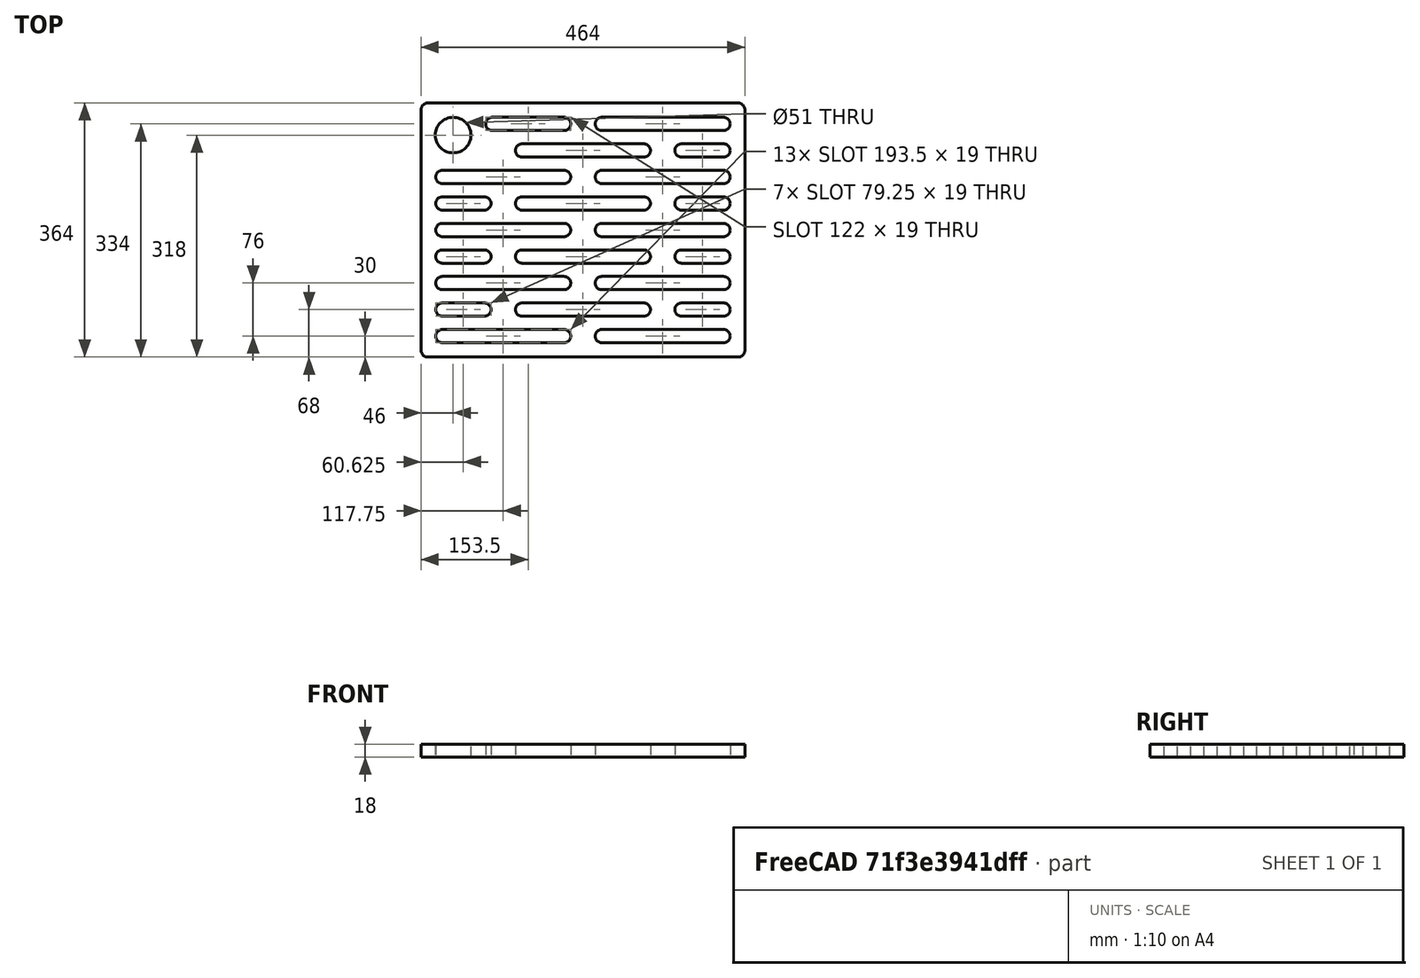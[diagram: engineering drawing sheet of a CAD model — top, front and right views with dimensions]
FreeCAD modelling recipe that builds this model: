
FCSTD DOCUMENT  (FreeCAD 0.18R4 (GitTag))
Label: shelf
License: All rights reserved
LicenseURL: http://en.wikipedia.org/wiki/All_rights_reserved
objects: Sketcher::SketchObject×1, PartDesign::Pad×1, PartDesign::Body×1
note: 4 computed .brp shape members not serialized (recipe doc carries the construction recipe); baked Part::Feature solids carry a one-line shape summary decoded from their .brp

FEATURE [Sketcher::SketchObject] Sketch
  MapMode = 5
  Support = -> [XY_Plane]
  sketch-geometry (93):
    g0: ArcOfCircle CenterX=-9.5 CenterY=9.5 CenterZ=0 NormalX=0 NormalY=0 NormalZ=1 AngleXU=0 Radius=9.5 StartAngle=4.71239 EndAngle=6.28319
    g1: ArcOfCircle CenterX=-9.5 CenterY=354.5 CenterZ=0 NormalX=0 NormalY=0 NormalZ=1 AngleXU=0 Radius=9.5 StartAngle=2.54933e-09 EndAngle=1.5708
    g2: ArcOfCircle CenterX=-454.5 CenterY=354.5 CenterZ=0 NormalX=0 NormalY=0 NormalZ=1 AngleXU=0 Radius=9.5 StartAngle=1.5708 EndAngle=3.14159
    g3: ArcOfCircle CenterX=-454.5 CenterY=9.5 CenterZ=0 NormalX=0 NormalY=0 NormalZ=1 AngleXU=0 Radius=9.5 StartAngle=3.14159 EndAngle=4.71239
    g4: LineSegment StartX=-454.5 StartY=0 StartZ=0 EndX=-9.5 EndY=0 EndZ=0
    g5: LineSegment StartX=0 StartY=9.5 StartZ=0 EndX=0 EndY=354.5 EndZ=0
    g6: LineSegment StartX=-9.5 StartY=364 StartZ=0 EndX=-454.5 EndY=364 EndZ=0
    g7: LineSegment StartX=-464 StartY=354.5 StartZ=0 EndX=-464 EndY=9.5 EndZ=0
    g8: Circle CenterX=-418 CenterY=318 CenterZ=0 NormalX=0 NormalY=0 NormalZ=1 AngleXU=0 Radius=25.5
    g9: ArcOfCircle CenterX=-205 CenterY=30 CenterZ=0 NormalX=0 NormalY=0 NormalZ=1 AngleXU=0 Radius=9.5 StartAngle=1.5708 EndAngle=4.71239
    g10: ArcOfCircle CenterX=-30.5 CenterY=30 CenterZ=0 NormalX=0 NormalY=0 NormalZ=1 AngleXU=0 Radius=9.5 StartAngle=4.71239 EndAngle=7.85398
    g11: LineSegment StartX=-205 StartY=20.5 StartZ=0 EndX=-30.5 EndY=20.5 EndZ=0
    g12: LineSegment StartX=-205 StartY=39.5 StartZ=0 EndX=-30.5 EndY=39.5 EndZ=0
    g13: ArcOfCircle CenterX=-90.75 CenterY=68 CenterZ=0 NormalX=0 NormalY=0 NormalZ=1 AngleXU=0 Radius=9.5 StartAngle=1.5708 EndAngle=4.71239
    g14: ArcOfCircle CenterX=-30.5 CenterY=68 CenterZ=0 NormalX=0 NormalY=0 NormalZ=1 AngleXU=0 Radius=9.5 StartAngle=4.71239 EndAngle=7.85398
    g15: LineSegment StartX=-90.75 StartY=58.5 StartZ=0 EndX=-30.5 EndY=58.5 EndZ=0
    g16: LineSegment StartX=-90.75 StartY=77.5 StartZ=0 EndX=-30.5 EndY=77.5 EndZ=0
    g17: ArcOfCircle CenterX=-205 CenterY=106 CenterZ=0 NormalX=0 NormalY=0 NormalZ=1 AngleXU=0 Radius=9.5 StartAngle=1.5708 EndAngle=4.71239
    g18: ArcOfCircle CenterX=-30.5 CenterY=106 CenterZ=0 NormalX=0 NormalY=0 NormalZ=1 AngleXU=0 Radius=9.5 StartAngle=4.71239 EndAngle=7.85398
    g19: LineSegment StartX=-205 StartY=96.5 StartZ=0 EndX=-30.5 EndY=96.5 EndZ=0
    g20: LineSegment StartX=-205 StartY=115.5 StartZ=0 EndX=-30.5 EndY=115.5 EndZ=0
    g21: ArcOfCircle CenterX=-90.75 CenterY=144 CenterZ=0 NormalX=0 NormalY=0 NormalZ=1 AngleXU=0 Radius=9.5 StartAngle=1.5708 EndAngle=4.71239
    g22: ArcOfCircle CenterX=-30.5 CenterY=144 CenterZ=0 NormalX=0 NormalY=0 NormalZ=1 AngleXU=0 Radius=9.5 StartAngle=4.71239 EndAngle=7.85398
    g23: LineSegment StartX=-90.75 StartY=134.5 StartZ=0 EndX=-30.5 EndY=134.5 EndZ=0
    g24: LineSegment StartX=-90.75 StartY=153.5 StartZ=0 EndX=-30.5 EndY=153.5 EndZ=0
    g25: ArcOfCircle CenterX=-205 CenterY=182 CenterZ=0 NormalX=0 NormalY=0 NormalZ=1 AngleXU=0 Radius=9.5 StartAngle=1.5708 EndAngle=4.71239
    g26: ArcOfCircle CenterX=-30.5 CenterY=182 CenterZ=0 NormalX=0 NormalY=0 NormalZ=1 AngleXU=0 Radius=9.5 StartAngle=4.71239 EndAngle=7.85398
    g27: LineSegment StartX=-205 StartY=172.5 StartZ=0 EndX=-30.5 EndY=172.5 EndZ=0
    g28: LineSegment StartX=-205 StartY=191.5 StartZ=0 EndX=-30.5 EndY=191.5 EndZ=0
    g29: ArcOfCircle CenterX=-90.75 CenterY=220 CenterZ=0 NormalX=0 NormalY=0 NormalZ=1 AngleXU=0 Radius=9.5 StartAngle=1.5708 EndAngle=4.71239
    g30: ArcOfCircle CenterX=-30.5 CenterY=220 CenterZ=0 NormalX=0 NormalY=0 NormalZ=1 AngleXU=0 Radius=9.5 StartAngle=4.71239 EndAngle=7.85398
    g31: LineSegment StartX=-90.75 StartY=210.5 StartZ=0 EndX=-30.5 EndY=210.5 EndZ=0
    g32: LineSegment StartX=-90.75 StartY=229.5 StartZ=0 EndX=-30.5 EndY=229.5 EndZ=0
    g33: ArcOfCircle CenterX=-205 CenterY=258 CenterZ=0 NormalX=0 NormalY=0 NormalZ=1 AngleXU=0 Radius=9.5 StartAngle=1.5708 EndAngle=4.71239
    g34: ArcOfCircle CenterX=-30.5 CenterY=258 CenterZ=0 NormalX=0 NormalY=0 NormalZ=1 AngleXU=0 Radius=9.5 StartAngle=4.71239 EndAngle=7.85398
    g35: LineSegment StartX=-205 StartY=248.5 StartZ=0 EndX=-30.5 EndY=248.5 EndZ=0
    g36: LineSegment StartX=-205 StartY=267.5 StartZ=0 EndX=-30.5 EndY=267.5 EndZ=0
    g37: ArcOfCircle CenterX=-90.75 CenterY=296 CenterZ=0 NormalX=0 NormalY=0 NormalZ=1 AngleXU=0 Radius=9.5 StartAngle=1.5708 EndAngle=4.71239
    g38: ArcOfCircle CenterX=-30.5 CenterY=296 CenterZ=0 NormalX=0 NormalY=0 NormalZ=1 AngleXU=0 Radius=9.5 StartAngle=4.71239 EndAngle=7.85398
    g39: LineSegment StartX=-90.75 StartY=286.5 StartZ=0 EndX=-30.5 EndY=286.5 EndZ=0
    g40: LineSegment StartX=-90.75 StartY=305.5 StartZ=0 EndX=-30.5 EndY=305.5 EndZ=0
    g41: ArcOfCircle CenterX=-259 CenterY=30 CenterZ=0 NormalX=0 NormalY=0 NormalZ=1 AngleXU=0 Radius=9.5 StartAngle=4.71239 EndAngle=7.85398
    g42: ArcOfCircle CenterX=-433.5 CenterY=30 CenterZ=0 NormalX=0 NormalY=0 NormalZ=1 AngleXU=0 Radius=9.5 StartAngle=1.5708 EndAngle=4.71239
    g43: LineSegment StartX=-259 StartY=39.5 StartZ=0 EndX=-433.5 EndY=39.5 EndZ=0
    g44: LineSegment StartX=-259 StartY=20.5 StartZ=0 EndX=-433.5 EndY=20.5 EndZ=0
    g45: ArcOfCircle CenterX=-433.5 CenterY=68 CenterZ=0 NormalX=0 NormalY=0 NormalZ=1 AngleXU=0 Radius=9.5 StartAngle=1.5708 EndAngle=4.71239
    g46: ArcOfCircle CenterX=-373.25 CenterY=68 CenterZ=0 NormalX=0 NormalY=0 NormalZ=1 AngleXU=0 Radius=9.5 StartAngle=4.71239 EndAngle=7.85398
    g47: LineSegment StartX=-433.5 StartY=58.5 StartZ=0 EndX=-373.25 EndY=58.5 EndZ=0
    g48: LineSegment StartX=-433.5 StartY=77.5 StartZ=0 EndX=-373.25 EndY=77.5 EndZ=0
    g49: ArcOfCircle CenterX=-319.25 CenterY=68 CenterZ=0 NormalX=0 NormalY=0 NormalZ=1 AngleXU=0 Radius=9.5 StartAngle=1.5708 EndAngle=4.71239
    g50: ArcOfCircle CenterX=-144.75 CenterY=68 CenterZ=0 NormalX=0 NormalY=0 NormalZ=1 AngleXU=0 Radius=9.5 StartAngle=4.71239 EndAngle=7.85398
    g51: LineSegment StartX=-319.25 StartY=58.5 StartZ=0 EndX=-144.75 EndY=58.5 EndZ=0
    g52: LineSegment StartX=-319.25 StartY=77.5 StartZ=0 EndX=-144.75 EndY=77.5 EndZ=0
    g53: ArcOfCircle CenterX=-433.5 CenterY=106 CenterZ=0 NormalX=0 NormalY=0 NormalZ=1 AngleXU=0 Radius=9.5 StartAngle=1.5708 EndAngle=4.71239
    g54: ArcOfCircle CenterX=-259 CenterY=106 CenterZ=0 NormalX=0 NormalY=0 NormalZ=1 AngleXU=0 Radius=9.5 StartAngle=4.71239 EndAngle=7.85398
    g55: LineSegment StartX=-433.5 StartY=96.5 StartZ=0 EndX=-259 EndY=96.5 EndZ=0
    g56: LineSegment StartX=-433.5 StartY=115.5 StartZ=0 EndX=-259 EndY=115.5 EndZ=0
    g57: ArcOfCircle CenterX=-319.25 CenterY=144 CenterZ=0 NormalX=0 NormalY=0 NormalZ=1 AngleXU=0 Radius=9.5 StartAngle=1.5708 EndAngle=4.71239
    g58: ArcOfCircle CenterX=-144.75 CenterY=144 CenterZ=0 NormalX=0 NormalY=0 NormalZ=1 AngleXU=0 Radius=9.5 StartAngle=4.71239 EndAngle=7.85398
    g59: LineSegment StartX=-319.25 StartY=134.5 StartZ=0 EndX=-144.75 EndY=134.5 EndZ=0
    g60: LineSegment StartX=-319.25 StartY=153.5 StartZ=0 EndX=-144.75 EndY=153.5 EndZ=0
    g61: ArcOfCircle CenterX=-373.25 CenterY=144 CenterZ=0 NormalX=0 NormalY=0 NormalZ=1 AngleXU=0 Radius=9.5 StartAngle=4.71239 EndAngle=7.85398
    g62: ArcOfCircle CenterX=-433.5 CenterY=144 CenterZ=0 NormalX=0 NormalY=0 NormalZ=1 AngleXU=0 Radius=9.5 StartAngle=1.5708 EndAngle=4.71239
    g63: LineSegment StartX=-373.25 StartY=153.5 StartZ=0 EndX=-433.5 EndY=153.5 EndZ=0
    g64: LineSegment StartX=-373.25 StartY=134.5 StartZ=0 EndX=-433.5 EndY=134.5 EndZ=0
    g65: ArcOfCircle CenterX=-259 CenterY=182 CenterZ=0 NormalX=0 NormalY=0 NormalZ=1 AngleXU=0 Radius=9.5 StartAngle=4.71239 EndAngle=7.85398
    g66: ArcOfCircle CenterX=-433.5 CenterY=182 CenterZ=0 NormalX=0 NormalY=0 NormalZ=1 AngleXU=0 Radius=9.5 StartAngle=1.5708 EndAngle=4.71239
    g67: LineSegment StartX=-259 StartY=191.5 StartZ=0 EndX=-433.5 EndY=191.5 EndZ=0
    g68: LineSegment StartX=-259 StartY=172.5 StartZ=0 EndX=-433.5 EndY=172.5 EndZ=0
    g69: ArcOfCircle CenterX=-144.75 CenterY=220 CenterZ=0 NormalX=0 NormalY=0 NormalZ=1 AngleXU=0 Radius=9.5 StartAngle=4.71239 EndAngle=7.85398
    g70: ArcOfCircle CenterX=-319.25 CenterY=220 CenterZ=0 NormalX=0 NormalY=0 NormalZ=1 AngleXU=0 Radius=9.5 StartAngle=1.5708 EndAngle=4.71239
    g71: LineSegment StartX=-144.75 StartY=229.5 StartZ=0 EndX=-319.25 EndY=229.5 EndZ=0
    g72: LineSegment StartX=-144.75 StartY=210.5 StartZ=0 EndX=-319.25 EndY=210.5 EndZ=0
    g73: ArcOfCircle CenterX=-373.25 CenterY=220 CenterZ=0 NormalX=0 NormalY=0 NormalZ=1 AngleXU=0 Radius=9.5 StartAngle=4.71239 EndAngle=7.85398
    g74: ArcOfCircle CenterX=-433.5 CenterY=220 CenterZ=0 NormalX=0 NormalY=0 NormalZ=1 AngleXU=0 Radius=9.5 StartAngle=1.5708 EndAngle=4.71239
    g75: LineSegment StartX=-373.25 StartY=229.5 StartZ=0 EndX=-433.5 EndY=229.5 EndZ=0
    g76: LineSegment StartX=-373.25 StartY=210.5 StartZ=0 EndX=-433.5 EndY=210.5 EndZ=0
    g77: ArcOfCircle CenterX=-259 CenterY=258 CenterZ=0 NormalX=0 NormalY=0 NormalZ=1 AngleXU=0 Radius=9.5 StartAngle=4.71239 EndAngle=7.85398
    g78: ArcOfCircle CenterX=-433.5 CenterY=258 CenterZ=0 NormalX=0 NormalY=0 NormalZ=1 AngleXU=0 Radius=9.5 StartAngle=1.5708 EndAngle=4.71239
    g79: LineSegment StartX=-259 StartY=267.5 StartZ=0 EndX=-433.5 EndY=267.5 EndZ=0
    g80: LineSegment StartX=-259 StartY=248.5 StartZ=0 EndX=-433.5 EndY=248.5 EndZ=0
    g81: ArcOfCircle CenterX=-319.25 CenterY=296 CenterZ=0 NormalX=0 NormalY=0 NormalZ=1 AngleXU=0 Radius=9.5 StartAngle=1.5708 EndAngle=4.71239
    g82: ArcOfCircle CenterX=-144.75 CenterY=296 CenterZ=0 NormalX=0 NormalY=0 NormalZ=1 AngleXU=0 Radius=9.5 StartAngle=4.71239 EndAngle=7.85398
    g83: LineSegment StartX=-319.25 StartY=286.5 StartZ=0 EndX=-144.75 EndY=286.5 EndZ=0
    g84: LineSegment StartX=-319.25 StartY=305.5 StartZ=0 EndX=-144.75 EndY=305.5 EndZ=0
    g85: ArcOfCircle CenterX=-30.5 CenterY=334 CenterZ=0 NormalX=0 NormalY=0 NormalZ=1 AngleXU=0 Radius=9.5 StartAngle=4.71239 EndAngle=7.85398
    g86: ArcOfCircle CenterX=-205 CenterY=334 CenterZ=0 NormalX=0 NormalY=0 NormalZ=1 AngleXU=0 Radius=9.5 StartAngle=1.5708 EndAngle=4.71239
    g87: LineSegment StartX=-30.5 StartY=343.5 StartZ=0 EndX=-205 EndY=343.5 EndZ=0
    g88: LineSegment StartX=-30.5 StartY=324.5 StartZ=0 EndX=-205 EndY=324.5 EndZ=0
    g89: ArcOfCircle CenterX=-259 CenterY=334 CenterZ=0 NormalX=0 NormalY=0 NormalZ=1 AngleXU=0 Radius=9.5 StartAngle=4.71239 EndAngle=7.85398
    g90: ArcOfCircle CenterX=-362 CenterY=334 CenterZ=0 NormalX=0 NormalY=0 NormalZ=1 AngleXU=0 Radius=9.5 StartAngle=1.5708 EndAngle=4.71239
    g91: LineSegment StartX=-259 StartY=343.5 StartZ=0 EndX=-362 EndY=343.5 EndZ=0
    g92: LineSegment StartX=-259 StartY=324.5 StartZ=0 EndX=-362 EndY=324.5 EndZ=0
  constraints (241):
    c: Horizontal(g6)
    c: Horizontal(g4)
    c: Vertical(g5)
    c: Vertical(g7)
    c: Coincident(g6,g1)
    c: Coincident(g1,g5)
    c: Coincident(g0,g5)
    c: Coincident(g0,g4)
    c: Coincident(g4,g3)
    c: Coincident(g3,g7)
    c: Coincident(g2,g6)
    c: Coincident(g2,g7)
    c: DistanceX(g0,g0) = 9.5
    c: DistanceY(g0,g0) = 9.5
    c: Radius(g0) = 9.5
    c: DistanceX(g1,g1) = 9.5
    c: DistanceY(g1,g1) = 9.5
    c: Radius(g1) = 9.5
    c: DistanceX(g2,g2) = 9.5
    c: DistanceY(g2,g2) = 9.5
    c: Radius(g2) = 9.5
    c: DistanceX(g3,g3) = 9.5
    c: DistanceY(g3,g3) = 9.5
    c: Radius(g3) = 9.5
    c: DistanceX(g0,g-1) = 0
    c: DistanceY(g-1,g0) = 0
    c: Diameter(g8) = 51
    c: DistanceX(g3,g0) = 464
    c: DistanceY(g0,g1) = 364
    c: DistanceX(g2,g8) = 46
    c: Tangent(g9,g12) = 1.5708
    c: Tangent(g9,g11) = -1.5708
    c: Tangent(g11,g10) = -1.5708
    c: Tangent(g12,g10) = 1.5708
    c: Horizontal(g11)
    c: Equal(g9,g10)
    c: Tangent(g13,g16) = 1.5708
    c: Tangent(g13,g15) = -1.5708
    c: Tangent(g15,g14) = -1.5708
    c: Tangent(g16,g14) = 1.5708
    c: Horizontal(g15)
    c: Equal(g13,g14)
    c: Tangent(g17,g20) = 1.5708
    c: Tangent(g17,g19) = -1.5708
    c: Tangent(g19,g18) = -1.5708
    c: Tangent(g20,g18) = 1.5708
    c: Horizontal(g19)
    c: Equal(g17,g18)
    c: Tangent(g21,g24) = 1.5708
    c: Tangent(g21,g23) = -1.5708
    c: Tangent(g23,g22) = -1.5708
    c: Tangent(g24,g22) = 1.5708
    c: Horizontal(g23)
    c: Equal(g21,g22)
    c: Tangent(g25,g28) = 1.5708
    c: Tangent(g25,g27) = -1.5708
    c: Tangent(g27,g26) = -1.5708
    c: Tangent(g28,g26) = 1.5708
    c: Horizontal(g27)
    c: Equal(g25,g26)
    c: Tangent(g29,g32) = 1.5708
    c: Tangent(g29,g31) = -1.5708
    c: Tangent(g31,g30) = -1.5708
    c: Tangent(g32,g30) = 1.5708
    c: Horizontal(g31)
    c: Equal(g29,g30)
    c: Tangent(g33,g36) = 1.5708
    c: Tangent(g33,g35) = -1.5708
    c: Tangent(g35,g34) = -1.5708
    c: Tangent(g36,g34) = 1.5708
    c: Horizontal(g35)
    c: Equal(g33,g34)
    c: DistanceY(g10,g10) = 19
    c: DistanceY(g14,g14) = 19
    c: DistanceY(g18,g18) = 19
    c: DistanceY(g22,g22) = 19
    c: DistanceY(g26,g26) = 19
    c: DistanceY(g30,g30) = 19
    c: DistanceY(g34,g34) = 19
    c: DistanceY(g10,g14) = 19
    c: DistanceY(g14,g18) = 19
    c: DistanceY(g18,g22) = 19
    c: DistanceY(g22,g26) = 19
    c: DistanceY(g26,g30) = 19
    c: DistanceY(g30,g34) = 19
    c: Tangent(g37,g40) = 1.5708
    c: Tangent(g37,g39) = -1.5708
    c: Tangent(g39,g38) = -1.5708
    c: Tangent(g40,g38) = 1.5708
    c: Horizontal(g39)
    c: Equal(g37,g38)
    c: DistanceY(g34,g38) = 19
    c: DistanceY(g38,g38) = 19
    c: DistanceY(g0,g10) = 20.5
    c: DistanceX(g10,g0) = 30.5
    c: DistanceX(g14,g10) = 0
    c: DistanceX(g18,g14) = 0
    c: DistanceX(g22,g18) = 0
    c: DistanceX(g26,g22) = 0
    c: DistanceX(g26,g30) = 0
    c: DistanceX(g34,g30) = 0
    c: DistanceX(g38,g34) = 0
    c: Tangent(g41,g44) = 1.5708
    c: Tangent(g41,g43) = -1.5708
    c: Tangent(g43,g42) = -1.5708
    c: Tangent(g44,g42) = 1.5708
    c: Horizontal(g43)
    c: Equal(g41,g42)
    c: DistanceY(g42,g42) = 19
    c: DistanceY(g3,g42) = 20.5
    c: DistanceX(g3,g42) = 30.5
    c: DistanceX(g9,g10) = 174.5
    c: DistanceX(g44,g44) = 174.5
    c: Tangent(g45,g48) = 1.5708
    c: Tangent(g45,g47) = -1.5708
    c: Tangent(g47,g46) = -1.5708
    c: Tangent(g48,g46) = 1.5708
    c: Horizontal(g47)
    c: Equal(g45,g46)
    c: Tangent(g49,g52) = 1.5708
    c: Tangent(g49,g51) = -1.5708
    c: Tangent(g51,g50) = -1.5708
    c: Tangent(g52,g50) = 1.5708
    c: Horizontal(g51)
    c: Equal(g49,g50)
    c: DistanceY(g9,g50) = 19
    c: DistanceY(g50,g50) = 19
    c: DistanceY(g42,g45) = 19
    c: DistanceY(g45,g45) = 19
    c: DistanceX(g45,g42) = 0
    c: DistanceX(g50,g13) = 54
    c: DistanceX(g46,g49) = 54
    c: DistanceX(g45,g46) = 60.25
    c: DistanceX(g52,g52) = 174.5
    c: Tangent(g53,g56) = 1.5708
    c: Tangent(g53,g55) = -1.5708
    c: Tangent(g55,g54) = -1.5708
    c: Tangent(g56,g54) = 1.5708
    c: Horizontal(g55)
    c: Equal(g53,g54)
    c: DistanceY(g45,g53) = 19
    c: DistanceY(g53,g53) = 19
    c: DistanceX(g53,g45) = 0
    c: DistanceX(g54,g41) = 0
    c: DistanceX(g9,g17) = 0
    c: Tangent(g57,g60) = 1.5708
    c: Tangent(g57,g59) = -1.5708
    c: Tangent(g59,g58) = -1.5708
    c: Tangent(g60,g58) = 1.5708
    c: Horizontal(g59)
    c: Equal(g57,g58)
    c: Tangent(g61,g64) = 1.5708
    c: Tangent(g61,g63) = -1.5708
    c: Tangent(g63,g62) = -1.5708
    c: Tangent(g64,g62) = 1.5708
    c: Horizontal(g63)
    c: Equal(g61,g62)
    c: Tangent(g65,g68) = 1.5708
    c: Tangent(g65,g67) = -1.5708
    c: Tangent(g67,g66) = -1.5708
    c: Tangent(g68,g66) = 1.5708
    c: Horizontal(g67)
    c: Equal(g65,g66)
    c: Tangent(g69,g72) = 1.5708
    c: Tangent(g69,g71) = -1.5708
    c: Tangent(g71,g70) = -1.5708
    c: Tangent(g72,g70) = 1.5708
    c: Horizontal(g71)
    c: Equal(g69,g70)
    c: Tangent(g73,g76) = 1.5708
    c: Tangent(g73,g75) = -1.5708
    c: Tangent(g75,g74) = -1.5708
    c: Tangent(g76,g74) = 1.5708
    c: Horizontal(g75)
    c: Equal(g73,g74)
    c: Tangent(g77,g80) = 1.5708
    c: Tangent(g77,g79) = -1.5708
    c: Tangent(g79,g78) = -1.5708
    c: Tangent(g80,g78) = 1.5708
    c: Horizontal(g79)
    c: Equal(g77,g78)
    c: DistanceY(g58,g58) = 19
    c: DistanceY(g58,g21) = 0
    c: DistanceY(g57,g61) = 0
    c: DistanceY(g61,g61) = 19
    c: DistanceX(g62,g53) = 0
    c: DistanceX(g46,g61) = 0
    c: DistanceX(g49,g57) = 0
    c: DistanceX(g50,g58) = 0
    c: DistanceX(g21,g13) = 0
    c: DistanceY(g62,g66) = 19
    c: DistanceY(g66,g66) = 19
    c: DistanceX(g17,g25) = 0
    c: DistanceX(g65,g54) = 0
    c: DistanceY(g66,g74) = 19
    c: DistanceY(g74,g74) = 19
    c: DistanceY(g70,g70) = 19
    c: DistanceY(g70,g73) = 0
    c: DistanceX(g61,g73) = 0
    c: DistanceX(g57,g70) = 0
    c: DistanceX(g69,g58) = 0
    c: DistanceX(g29,g21) = 0
    c: DistanceY(g78,g78) = 19
    c: DistanceY(g33,g77) = 0
    c: DistanceX(g33,g25) = 0
    c: DistanceX(g65,g77) = 0
    c: Tangent(g81,g84) = 1.5708
    c: Tangent(g81,g83) = -1.5708
    c: Tangent(g83,g82) = -1.5708
    c: Tangent(g84,g82) = 1.5708
    c: Horizontal(g83)
    c: Equal(g81,g82)
    c: DistanceY(g82,g82) = 19
    c: DistanceY(g37,g82) = 0
    c: DistanceX(g29,g37) = 0
    c: DistanceX(g69,g82) = 0
    c: Tangent(g85,g88) = 1.5708
    c: Tangent(g85,g87) = -1.5708
    c: Tangent(g87,g86) = -1.5708
    c: Tangent(g88,g86) = 1.5708
    c: Horizontal(g87)
    c: Equal(g85,g86)
    c: Tangent(g89,g92) = 1.5708
    c: Tangent(g89,g91) = -1.5708
    c: Tangent(g91,g90) = -1.5708
    c: Tangent(g92,g90) = 1.5708
    c: Horizontal(g91)
    c: Equal(g89,g90)
    c: DistanceY(g38,g85) = 19
    c: DistanceY(g85,g85) = 19
    c: DistanceX(g38,g85) = 0
    c: DistanceX(g33,g86) = 0
    c: DistanceX(g77,g89) = 0
    c: DistanceY(g89,g86) = 0
    c: DistanceY(g89,g89) = 19
    c: DistanceY(g8,g2) = 46
    c: DistanceX(g62,g66) = 0
    c: DistanceX(g66,g74) = 0
    c: DistanceX(g74,g78) = 0
    c: DistanceX(g8,g90) = 56
    c: DistanceX(g81,g70) = 0
FEATURE [PartDesign::Pad] Pad
  Length = 18
  Length2 = 100
  Profile = -> Sketch
  Type = 0
FEATURE [PartDesign::Body] Body
  Group = -> [Sketch,Pad]
  Origin = -> Origin
  Tip = -> Pad
